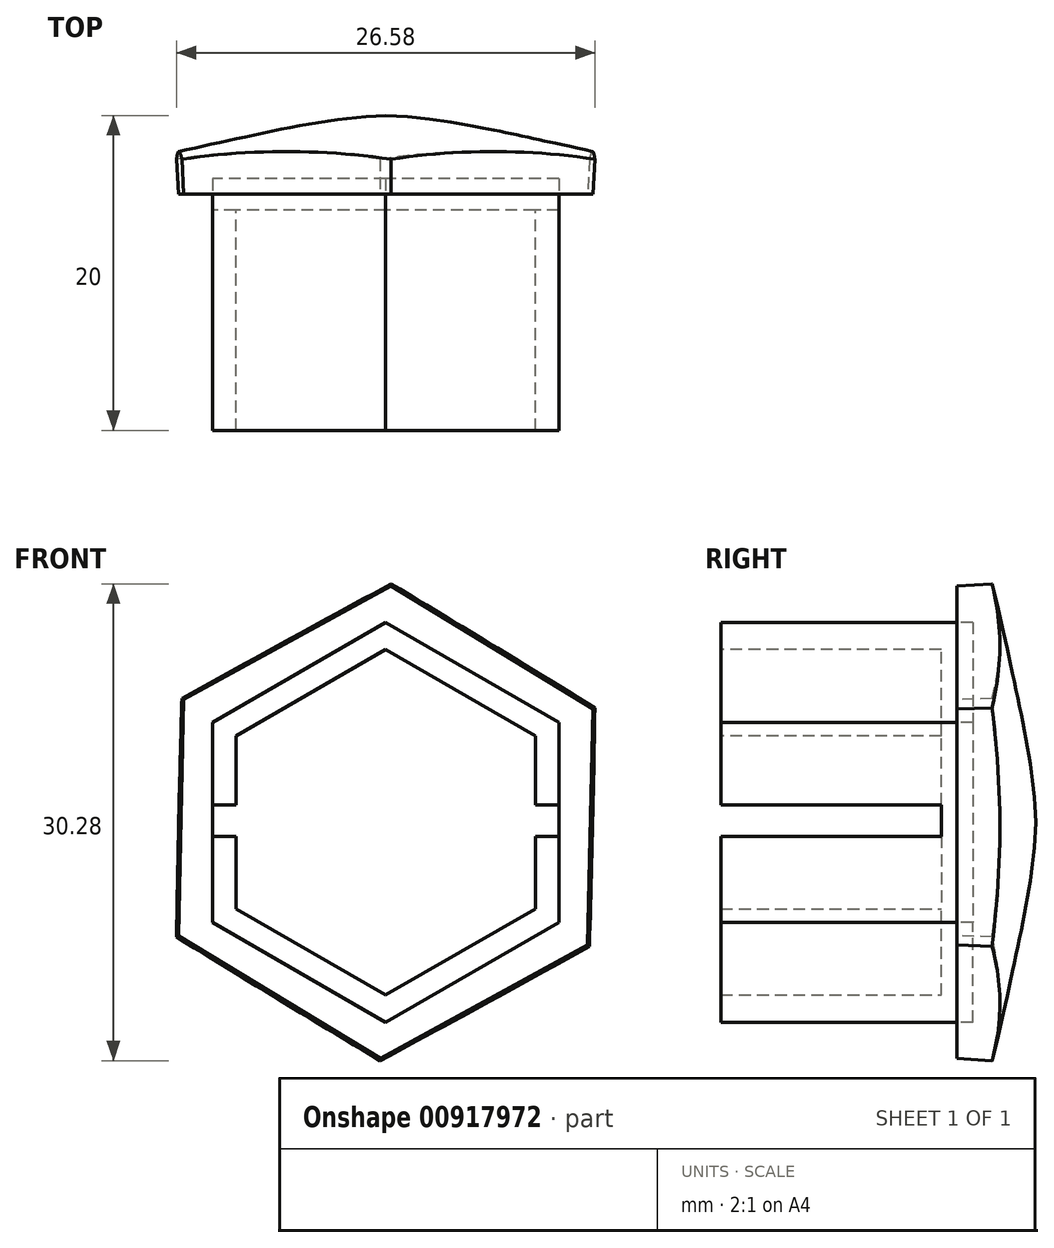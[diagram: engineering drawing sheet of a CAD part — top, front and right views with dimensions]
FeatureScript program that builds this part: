
annotation { "Feature Type Name" : "Feature", "Feature Type Description" : "" }
export const myFeature = defineFeature(function(context is Context, id is Id, definition is map)
    precondition{}
    {
        {
            var Q0;
            Q0=qCreatedBy(makeId("Front.planeOp"),FACE);
            var sketch = newSketch(context, id + "F0", { "sketchPlane" : qUnion([Q0])});
            skCircle(sketch, "E0.cCircle", {"center": v(0, 0) * mm, "radius": 12.7 * mm, "construction": true});
            skLineSegment(sketch, "E0.0", {"start": v(0, -12.7) * mm, "end": v(-11, -6.35) * mm});
            skLineSegment(sketch, "E0.1", {"start": v(-11, -6.35) * mm, "end": v(-11, 6.35) * mm});
            skLineSegment(sketch, "E0.2", {"start": v(-11, 6.35) * mm, "end": v(0, 12.7) * mm});
            skLineSegment(sketch, "E0.3", {"start": v(0, 12.7) * mm, "end": v(11, 6.35) * mm});
            skLineSegment(sketch, "E0.4", {"start": v(11, 6.35) * mm, "end": v(11, -6.35) * mm});
            skLineSegment(sketch, "E0.5", {"start": v(11, -6.35) * mm, "end": v(0, -12.7) * mm});
            skSolve(sketch);
        }
        {
            var Q0;
            Q0 = qSketchRegion(id + "F0", true);
            extrude(context, id + "F1", {"entities" : qUnion([Q0]), "depth" : 15 * mm, "offsetDistance" : 25 * mm});
        }
        {
            var Q0;
            Q0=makeQuery(id+"F1.opExtrude","CAP_FACE",FACE,{"disambiguationData":[OSD([sQuery(id+"F0.wireOp",EDGE,"E0.0"),sQuery(id+"F0.wireOp",EDGE,"E0.1"),sQuery(id+"F0.wireOp",EDGE,"E0.2"),sQuery(id+"F0.wireOp",EDGE,"E0.3"),sQuery(id+"F0.wireOp",EDGE,"E0.4"),sQuery(id+"F0.wireOp",EDGE,"E0.5")])],"isStart":false});
            shell(context, id + "F2", {"entities" : qUnion([Q0]), "thickness" : 1.5 * mm});
        }
        {
            var Q0;
            Q0=qCreatedBy(makeId("Top.planeOp"),FACE);
            var sketch = newSketch(context, id + "F3", { "sketchPlane" : qUnion([Q0])});
            skLineSegment(sketch, "E1", {"start": v(0, 0) * mm, "end": v(-16, 0) * mm});
            skLineSegment(sketch, "E2", {"start": v(-16, 0) * mm, "end": v(-16, 2) * mm});
            skFitSpline(sketch, "E3", {"points": [v(-16, 2) * mm, v(-9.06, 3.62) * mm, v(0, 5) * mm], "startDerivative": vector(14.24, 3.9) * mm, "endDerivative": vector(17.69, 0.53) * mm});
            skLineSegment(sketch, "E4", {"start": v(0, 5) * mm, "end": v(0, 0) * mm});
            skSolve(sketch);
        }
        {
            var Q0;
            Q0=makeQuery(id+"F3.imprint","IMPRINT",FACE,{"disambiguationData":[TD([[makeQuery(id+"F3.imprint","IMPRINT",EDGE,{"derivedFrom":sQuery(id+"F3.wireOp",EDGE,"E1")}),-1.0]])]});
            var Q1;
            Q1=sQuery(id+"F3.wireOp",EDGE,"E4");
            revolve(context, id + "F4", {"operationType" : NewBodyOperationType.ADD, "surfaceOperationType" : NewSurfaceOperationType.NEW, "entities" : qUnion([Q0]), "axis" : qUnion([Q1]), "revolveType" : RevolveType.FULL});
        }
        {
            var Q0;
            Q0=qCreatedBy(makeId("Front.planeOp"),FACE);
            var sketch = newSketch(context, id + "F5", { "sketchPlane" : qUnion([Q0])});
            skCircle(sketch, "E5.cCircle", {"center": v(0, 0) * mm, "radius": 15.01 * mm, "construction": true});
            skLineSegment(sketch, "E5.0", {"start": v(12.83, -7.8) * mm, "end": v(-0.34, -15) * mm});
            skLineSegment(sketch, "E5.1", {"start": v(-0.34, -15) * mm, "end": v(-13.17, -7.2) * mm});
            skLineSegment(sketch, "E5.2", {"start": v(-13.17, -7.2) * mm, "end": v(-12.83, 7.8) * mm});
            skLineSegment(sketch, "E5.3", {"start": v(-12.83, 7.8) * mm, "end": v(0.34, 15) * mm});
            skLineSegment(sketch, "E5.4", {"start": v(0.34, 15) * mm, "end": v(13.17, 7.2) * mm});
            skLineSegment(sketch, "E5.5", {"start": v(13.17, 7.2) * mm, "end": v(12.83, -7.8) * mm});
            skSolve(sketch);
        }
        {
            var Q0;
            Q0=makeQuery(id+"F5.imprint","IMPRINT",FACE,{"disambiguationData":[TD([[makeQuery(id+"F5.imprint","IMPRINT",EDGE,{"derivedFrom":sQuery(id+"F5.wireOp",EDGE,"E5.0")}),-1.0]])]});
            extrude(context, id + "F6", {"entities" : qUnion([Q0]), "operationType" : NewBodyOperationType.INTERSECT, "oppositeDirection" : true, "depth" : 13.44 * mm, "offsetDistance" : 25 * mm, "hasDraft" : true, "draftAngle" : 3 * degree, "hasSecondDirection" : true, "secondDirectionOppositeDirection" : false, "secondDirectionDepth" : 18.5 * mm});
        }
        {
            var Q0;
            Q0=qCreatedBy(makeId("Front.planeOp"),FACE);
            var sketch = newSketch(context, id + "F7", { "sketchPlane" : qUnion([Q0])});
            skLineSegment(sketch, "E6.bottom", {"start": v(12.11, -0.89) * mm, "end": v(-12.2, -0.89) * mm});
            skLineSegment(sketch, "E6.top", {"start": v(12.11, 1.11) * mm, "end": v(-12.2, 1.11) * mm});
            skLineSegment(sketch, "E6.left", {"start": v(12.11, -0.89) * mm, "end": v(12.11, 1.11) * mm});
            skLineSegment(sketch, "E6.right", {"start": v(-12.2, -0.89) * mm, "end": v(-12.2, 1.11) * mm});
            skSolve(sketch);
        }
        {
            var Q0;
            Q0=makeQuery(id+"F7.imprint","IMPRINT",FACE,{"disambiguationData":[TD([[makeQuery(id+"F7.imprint","IMPRINT",EDGE,{"derivedFrom":sQuery(id+"F7.wireOp",EDGE,"E6.bottom")}),-1.0]])]});
            extrude(context, id + "F8", {"entities" : qUnion([Q0]), "operationType" : NewBodyOperationType.REMOVE, "depth" : 25 * mm, "offsetDistance" : 25 * mm});
        }
        {
            var Q0;
            {var subQ0=sQuery(id+"F0.wireOp",EDGE,"E0.5");var subQ1=sQuery(id+"F0.wireOp",EDGE,"E0.1");var subQ2=sQuery(id+"F0.wireOp",EDGE,"E0.4");var subQ3=sQuery(id+"F0.wireOp",EDGE,"E0.0");Q0=makeQuery(id+"F8.boolean.opBoolean","SPLIT",FACE,{"disambiguationData":[TD([makeQuery(id+"F2.opShell","OFFSET_FACE",FACE,{"disambiguationData":[OSD([subQ3])]})])],"derivedFrom":makeQuery(id+"F2.opShell","OFFSET_FACE",FACE,{"disambiguationData":[OSD([subQ3,subQ1,sQuery(id+"F0.wireOp",EDGE,"E0.2"),sQuery(id+"F0.wireOp",EDGE,"E0.3"),subQ2,subQ0])]})});}
            extrude(context, id + "F9", {"entities" : qUnion([Q0]), "operationType" : NewBodyOperationType.REMOVE, "oppositeDirection" : true, "depth" : 1 * mm, "offsetDistance" : 25 * mm});
        }
        {
            var Q0;
            {var subQ0=sQuery(id+"F0.wireOp",EDGE,"E0.4");var subQ1=sQuery(id+"F0.wireOp",EDGE,"E0.3");var subQ2=sQuery(id+"F0.wireOp",EDGE,"E0.2");var subQ3=sQuery(id+"F0.wireOp",EDGE,"E0.1");Q0=makeQuery(id+"F8.boolean.opBoolean","SPLIT",FACE,{"disambiguationData":[TD([makeQuery(id+"F2.opShell","OFFSET_FACE",FACE,{"disambiguationData":[OSD([subQ2])]})])],"derivedFrom":makeQuery(id+"F2.opShell","OFFSET_FACE",FACE,{"disambiguationData":[OSD([sQuery(id+"F0.wireOp",EDGE,"E0.0"),subQ3,subQ2,subQ1,subQ0,sQuery(id+"F0.wireOp",EDGE,"E0.5")])]})});}
            var Q1;
            Q1=makeQuery(id+"F0.imprint","IMPRINT",FACE,{"disambiguationData":[TD([[makeQuery(id+"F0.imprint","IMPRINT",EDGE,{"derivedFrom":sQuery(id+"F0.wireOp",EDGE,"E0.0")}),-1.0]])]});
            extrude(context, id + "F10", {"entities" : qUnion([Q0, Q1]), "operationType" : NewBodyOperationType.REMOVE, "oppositeDirection" : true, "depth" : 1 * mm, "offsetDistance" : 25 * mm});
        }
        {
            var Q0;
            Q0=makeQuery(id+"F0.imprint","IMPRINT",FACE,{"disambiguationData":[TD([[makeQuery(id+"F0.imprint","IMPRINT",EDGE,{"derivedFrom":sQuery(id+"F0.wireOp",EDGE,"E0.0")}),-1.0]])]});
            extrude(context, id + "F11", {"entities" : qUnion([Q0]), "operationType" : NewBodyOperationType.ADD, "depth" : 1 * mm, "offsetDistance" : 25 * mm});
        }
    });
